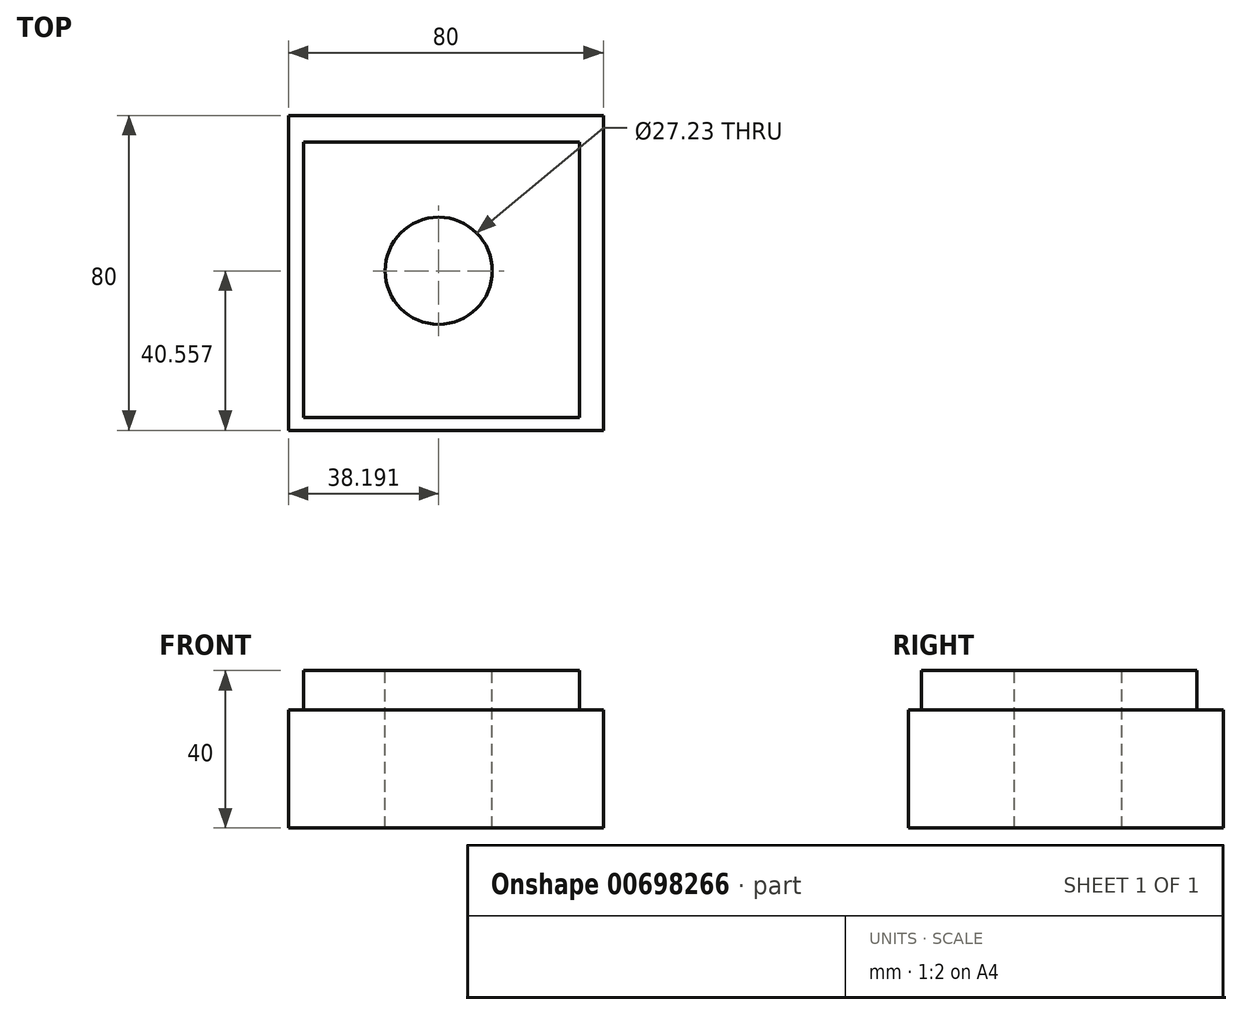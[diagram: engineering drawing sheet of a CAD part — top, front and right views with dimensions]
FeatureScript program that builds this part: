
annotation { "Feature Type Name" : "Feature", "Feature Type Description" : "" }
export const myFeature = defineFeature(function(context is Context, id is Id, definition is map)
    precondition{}
    {
        {
            var Q0;
            Q0=qCreatedBy(makeId("Top.planeOp"),FACE);
            var sketch = newSketch(context, id + "F0", { "sketchPlane" : qUnion([Q0])});
            skLineSegment(sketch, "E0.bottom", {"start": v(-30.05, 43.44) * mm, "end": v(49.95, 43.44) * mm});
            skLineSegment(sketch, "E0.top", {"start": v(-30.05, -36.56) * mm, "end": v(49.95, -36.56) * mm});
            skLineSegment(sketch, "E0.left", {"start": v(-30.05, 43.44) * mm, "end": v(-30.05, -36.56) * mm});
            skLineSegment(sketch, "E0.right", {"start": v(49.95, 43.44) * mm, "end": v(49.95, -36.56) * mm});
            skSolve(sketch);
        }
        {
            var Q0;
            Q0 = qSketchRegion(id + "F0", true);
            extrude(context, id + "F1", {"entities" : qUnion([Q0]), "depth" : 30 * mm, "offsetDistance" : 25 * mm});
        }
        {
            var Q0;
            Q0=makeQuery(id+"F1.opExtrude","CAP_FACE",FACE,{"disambiguationData":[OSD([sQuery(id+"F0.wireOp",EDGE,"E0.bottom"),sQuery(id+"F0.wireOp",EDGE,"E0.top"),sQuery(id+"F0.wireOp",EDGE,"E0.left"),sQuery(id+"F0.wireOp",EDGE,"E0.right")])],"isStart":false});
            var sketch = newSketch(context, id + "F2", { "sketchPlane" : qUnion([Q0])});
            skLineSegment(sketch, "E1.bottom", {"start": v(-26.12, 36.68) * mm, "end": v(43.88, 36.68) * mm});
            skLineSegment(sketch, "E1.top", {"start": v(-26.12, -33.32) * mm, "end": v(43.88, -33.32) * mm});
            skLineSegment(sketch, "E1.left", {"start": v(-26.12, 36.68) * mm, "end": v(-26.12, -33.32) * mm});
            skLineSegment(sketch, "E1.right", {"start": v(43.88, 36.68) * mm, "end": v(43.88, -33.32) * mm});
            skSolve(sketch);
        }
        {
            var Q0;
            Q0 = qSketchRegion(id + "F2", true);
            extrude(context, id + "F3", {"entities" : qUnion([Q0]), "operationType" : NewBodyOperationType.ADD, "depth" : 10 * mm, "offsetDistance" : 25 * mm});
        }
        {
            var Q0;
            Q0=makeQuery(id+"F3.opExtrude","CAP_FACE",FACE,{"disambiguationData":[OSD([sQuery(id+"F2.wireOp",EDGE,"E1.bottom"),sQuery(id+"F2.wireOp",EDGE,"E1.top"),sQuery(id+"F2.wireOp",EDGE,"E1.left"),sQuery(id+"F2.wireOp",EDGE,"E1.right")])],"isStart":false});
            var sketch = newSketch(context, id + "F4", { "sketchPlane" : qUnion([Q0])});
            skCircle(sketch, "E2", {"center": v(8.14, 4) * mm, "radius": 13.61 * mm});
            skSolve(sketch);
        }
        {
            var Q0;
            Q0 = qSketchRegion(id + "F4", true);
            extrude(context, id + "F5", {"entities" : qUnion([Q0]), "operationType" : NewBodyOperationType.REMOVE, "endBound" : BoundingType.THROUGH_ALL, "oppositeDirection" : true, "depth" : 40 * mm, "offsetDistance" : 25 * mm});
        }
    });
